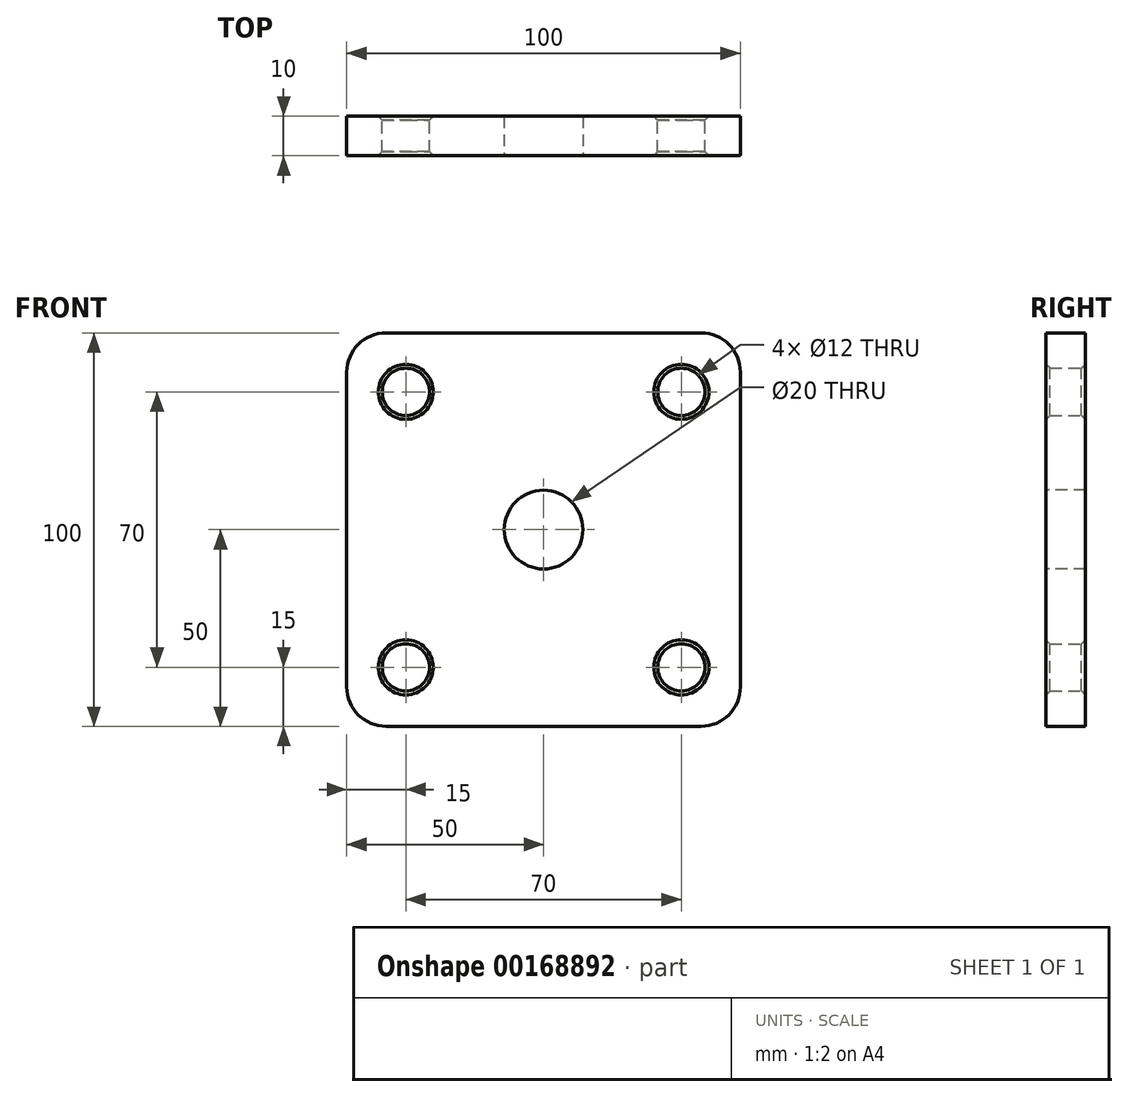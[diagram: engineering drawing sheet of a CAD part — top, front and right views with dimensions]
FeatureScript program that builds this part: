
annotation { "Feature Type Name" : "Feature", "Feature Type Description" : "" }
export const myFeature = defineFeature(function(context is Context, id is Id, definition is map)
    precondition{}
    {
        {
            var Q0;
            Q0=qCreatedBy(makeId("Front.planeOp"),FACE);
            var sketch = newSketch(context, id + "F0", { "sketchPlane" : qUnion([Q0])});
            skLineSegment(sketch, "E0.bottom", {"start": v(-50, -50) * mm, "end": v(50, -50) * mm});
            skLineSegment(sketch, "E0.top", {"start": v(-50, 50) * mm, "end": v(50, 50) * mm});
            skLineSegment(sketch, "E0.left", {"start": v(-50, -50) * mm, "end": v(-50, 50) * mm});
            skLineSegment(sketch, "E0.right", {"start": v(50, -50) * mm, "end": v(50, 50) * mm});
            skPoint(sketch, "E0.middle", {"position": v(0, 0) * mm});
            skCircle(sketch, "E1", {"center": v(-35, 35) * mm, "radius": 6 * mm});
            skCircle(sketch, "E2", {"center": v(35, 35) * mm, "radius": 6 * mm});
            skCircle(sketch, "E3", {"center": v(35, -35) * mm, "radius": 6 * mm});
            skCircle(sketch, "E4", {"center": v(-35, -35) * mm, "radius": 6 * mm});
            skSolve(sketch);
        }
        {
            var Q0;
            Q0=makeQuery(id+"F0.imprint","IMPRINT",FACE,{"disambiguationData":[TD([[makeQuery(id+"F0.imprint","IMPRINT",EDGE,{"derivedFrom":sQuery(id+"F0.wireOp",EDGE,"E0.bottom")}),1.0]])]});
            extrude(context, id + "F1", {"entities" : qUnion([Q0]), "depth" : 10 * mm});
        }
        {
            var Q0;
            Q0=makeQuery(id+"F1.opExtrude","CAP_FACE",FACE,{"disambiguationData":[OSD([sQuery(id+"F0.wireOp",EDGE,"E0.bottom"),sQuery(id+"F0.wireOp",EDGE,"E0.top"),sQuery(id+"F0.wireOp",EDGE,"E0.left"),sQuery(id+"F0.wireOp",EDGE,"E0.right"),sQuery(id+"F0.wireOp",EDGE,"E1"),sQuery(id+"F0.wireOp",EDGE,"E2"),sQuery(id+"F0.wireOp",EDGE,"E3"),sQuery(id+"F0.wireOp",EDGE,"E4")])],"isStart":false});
            var sketch = newSketch(context, id + "F2", { "sketchPlane" : qUnion([Q0])});
            skPoint(sketch, "E5", {"position": v(0, 0) * mm});
            skSolve(sketch);
        }
        {
            var Q0;
            Q0=sQuery(id+"F2.wireOp",VERTEX,"E5");
            var Q1;
            Q1=makeQuery(id+"F1.opExtrude","SWEPT_BODY",BODY,{"disambiguationData":[OSD([sQuery(id+"F0.wireOp",EDGE,"E0.bottom"),sQuery(id+"F0.wireOp",EDGE,"E0.top"),sQuery(id+"F0.wireOp",EDGE,"E0.left"),sQuery(id+"F0.wireOp",EDGE,"E0.right"),sQuery(id+"F0.wireOp",EDGE,"E1"),sQuery(id+"F0.wireOp",EDGE,"E2"),sQuery(id+"F0.wireOp",EDGE,"E3"),sQuery(id+"F0.wireOp",EDGE,"E4")])]});
            hole(context, id + "F3", {"style" : HoleStyle.SIMPLE, "endStyle" : HoleEndStyle.THROUGH, "standardTappedOrClearance" : lookupTablePath({ "standard" : "ISO", "size" : "20", "type" : "Drilled" }), "standardBlindInLast" : lookupTablePath({ "standard" : "ISO", "size" : "20", "type" : "Drilled" }), "holeDiameter" : 20 * mm, "locations" : qUnion([Q0]), "scope" : qUnion([Q1]), "isTappedThrough" : true});
        }
        {
            var Q0;
            Q0=makeQuery(id+"F1.opExtrude","SWEPT_EDGE",EDGE,{"disambiguationData":[OSD([sQuery(id+"F0.wireOp",EDGE,"E0.bottom"),sQuery(id+"F0.wireOp",EDGE,"E0.left")])]});
            var Q1;
            Q1=makeQuery(id+"F1.opExtrude","SWEPT_EDGE",EDGE,{"disambiguationData":[OSD([sQuery(id+"F0.wireOp",EDGE,"E0.bottom"),sQuery(id+"F0.wireOp",EDGE,"E0.right")])]});
            var Q2;
            Q2=makeQuery(id+"F1.opExtrude","SWEPT_EDGE",EDGE,{"disambiguationData":[OSD([sQuery(id+"F0.wireOp",EDGE,"E0.top"),sQuery(id+"F0.wireOp",EDGE,"E0.right")])]});
            var Q3;
            Q3=makeQuery(id+"F1.opExtrude","SWEPT_EDGE",EDGE,{"disambiguationData":[OSD([sQuery(id+"F0.wireOp",EDGE,"E0.top"),sQuery(id+"F0.wireOp",EDGE,"E0.left")])]});
            fillet(context, id + "F4", {"entities" : qUnion([Q0, Q1, Q2, Q3]), "radius" : 10 * mm, "tangentPropagation" : true, "allowEdgeOverflow" : false});
        }
        {
            var Q0;
            Q0=makeQuery(id+"F1.opExtrude","CAP_EDGE",EDGE,{"disambiguationData":[OSD([sQuery(id+"F0.wireOp",EDGE,"E1")])],"isStart":false});
            var Q1;
            Q1=makeQuery(id+"F1.opExtrude","CAP_EDGE",EDGE,{"disambiguationData":[OSD([sQuery(id+"F0.wireOp",EDGE,"E2")])],"isStart":false});
            var Q2;
            Q2=makeQuery(id+"F1.opExtrude","CAP_EDGE",EDGE,{"disambiguationData":[OSD([sQuery(id+"F0.wireOp",EDGE,"E3")])],"isStart":false});
            var Q3;
            Q3=makeQuery(id+"F1.opExtrude","CAP_EDGE",EDGE,{"disambiguationData":[OSD([sQuery(id+"F0.wireOp",EDGE,"E4")])],"isStart":false});
            var Q4;
            Q4=makeQuery(id+"F1.opExtrude","CAP_EDGE",EDGE,{"disambiguationData":[OSD([sQuery(id+"F0.wireOp",EDGE,"E1")])],"isStart":true});
            var Q5;
            Q5=makeQuery(id+"F1.opExtrude","CAP_EDGE",EDGE,{"disambiguationData":[OSD([sQuery(id+"F0.wireOp",EDGE,"E4")])],"isStart":true});
            var Q6;
            Q6=makeQuery(id+"F1.opExtrude","CAP_EDGE",EDGE,{"disambiguationData":[OSD([sQuery(id+"F0.wireOp",EDGE,"E3")])],"isStart":true});
            var Q7;
            Q7=makeQuery(id+"F1.opExtrude","CAP_EDGE",EDGE,{"disambiguationData":[OSD([sQuery(id+"F0.wireOp",EDGE,"E2")])],"isStart":true});
            var Q8;
            Q8=makeQuery(id+"F3.hole-0.boolean.opBoolean","COPY",EDGE,{"derivedFrom":makeQuery(id+"F3.hole-0.opRevolve","SWEPT_EDGE",EDGE,{"disambiguationData":[OSD([sQuery(id+"F3.hole-0.sketch.wireOp",EDGE,"core_line_2"),sQuery(id+"F3.hole-0.sketch.wireOp",EDGE,"core_line_3")])]})});
            var Q9;
            Q9=makeQuery(id+"F3.hole-0.boolean.opBoolean","INTERSECT",EDGE,{"derivedFrom":[makeQuery(id+"F1.opExtrude","CAP_FACE",FACE,{"disambiguationData":[OSD([sQuery(id+"F0.wireOp",EDGE,"E0.bottom"),sQuery(id+"F0.wireOp",EDGE,"E0.top"),sQuery(id+"F0.wireOp",EDGE,"E0.left"),sQuery(id+"F0.wireOp",EDGE,"E0.right"),sQuery(id+"F0.wireOp",EDGE,"E1"),sQuery(id+"F0.wireOp",EDGE,"E2"),sQuery(id+"F0.wireOp",EDGE,"E3"),sQuery(id+"F0.wireOp",EDGE,"E4")])],"isStart":true}),makeQuery(id+"F3.hole-0.opRevolve","SWEPT_FACE",FACE,{"disambiguationData":[OSD([sQuery(id+"F3.hole-0.sketch.wireOp",EDGE,"core_line_2")])]})]});
            chamfer(context, id + "F5", {"entities" : qUnion([Q0, Q1, Q2, Q3, Q4, Q5, Q6, Q7, Q8, Q9]), "width" : 1 * mm, "tangentPropagation" : true});
        }
    });
